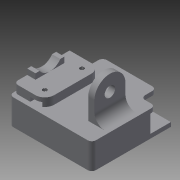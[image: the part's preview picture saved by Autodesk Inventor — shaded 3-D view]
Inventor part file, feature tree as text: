
AUTODESK INVENTOR PART (.ipt)
format: ipt  version: 2014 SP1 (Build 180222100, 222)  size: 295,936 bytes
history: native  units: mm
features: extrude x12, sketch x12, mirror x4, fillet x4, plane x2, hole x1
ambient origin geometry x8: Origin, YZ Plane, XZ Plane, XY Plane, X Axis, Y Axis, Z Axis, Center Point
bodies: Solid1 (feature_tree)
feature tree (35):
  extrude  "Extrusion1"  Depth=40.0mm
  extrude  "Extrusion2"  Depth=10.0mm
  extrude  "Extrusion3"  Depth=8.5mm TaperAngle=0.0deg
  mirror  "Mirror1"
  extrude  "Extrusion4"  Depth=2.0mm TaperAngle=0.0deg
  mirror  "Mirror2"
  extrude  "Extrusion5"  Depth=2.0mm TaperAngle=0.0deg
  extrude  "Extrusion6"  Depth=12.5mm
  extrude  "Extrusion7"  Depth=12.5mm
  fillet  "Fillet1"  Radius=18.25mm
  extrude  "Extrusion8"  Depth=3.0mm
  plane  "Work Plane1"
  extrude  "Extrusion9"  Depth=5.0mm
  plane  "Work Plane2"
  mirror  "Mirror3"
  hole  "Hole1"  [1 undecoded]
  extrude  "Extrusion10"  Depth=7.5mm
  extrude  "Extrusion11"  Depth=7.5mm
  extrude  "Extrusion12"  Depth=15.0mm
  mirror  "Mirror4"
  fillet  "Fillet2"  Radius=27.0mm
  fillet  "Fillet3"  Radius=4.0mm
  fillet  "Fillet4"  [1 undecoded]
  sketch  "Sketch1"  dims[d0=40.0mm d2=6.35mm]
  sketch  "Sketch2"  dims[d4=9.5mm d5=10.0mm]
  sketch  "Sketch4"  dims[d6=20.0mm d7=8.5mm d8=0.0mm]
  sketch  "Sketch5"  dims[d9=20.0mm d10=2.0mm d11=0.0mm]
  sketch  "Sketch6"  dims[d12=6.35mm d13=2.0mm d14=0.0mm]
  sketch  "Sketch7"  dims[d15=7.0mm d17=12.5mm]
  sketch  "Sketch9"  dims[d18=2.0mm d19=0.0mm d20=12.5mm d21=18.25mm d22=0.0mm]
  sketch  "Sketch10"  dims[d23=15.0mm d25=3.0mm]
  sketch  "Sketch11"  dims[d26=4.5mm d27=5.0mm]
  sketch  "Sketch12"  dims[d28=14.5mm d29=17.5mm d30=0.0mm]
  sketch  "Sketch13"  dims[d31=5.1mm d34=7.5mm]
  sketch  "Sketch14"  dims[d35=10.0mm d36=0.0mm d37=7.5mm d38=15.0mm d39=27.0mm d41=4.0mm d42=0.0mm d43=-2.0mm d44=5.0mm d45=4.5mm d46=9.0mm d47=2.0mm d48=0.0mm d49=4.5mm d50=18.0mm d51=2.013mm d52=6.0mm d53=4.0mm d54=2.0mm d55=90.0deg d56=4.0mm d57=20.594885mm d58=6.0mm d61=10.0mm d62=4.0mm d63=0.0mm d64=12.0mm d65=5.0mm d66=0.0mm d67=2.0mm d68=0.0mm d69=4.5mm d70=5.0mm d71=2.0mm]
note: 2 required parameter values undecoded (feature->parameter linkage not recoverable at this tier; creation-order binding heuristic only, values carry confidence <= 0.55)
